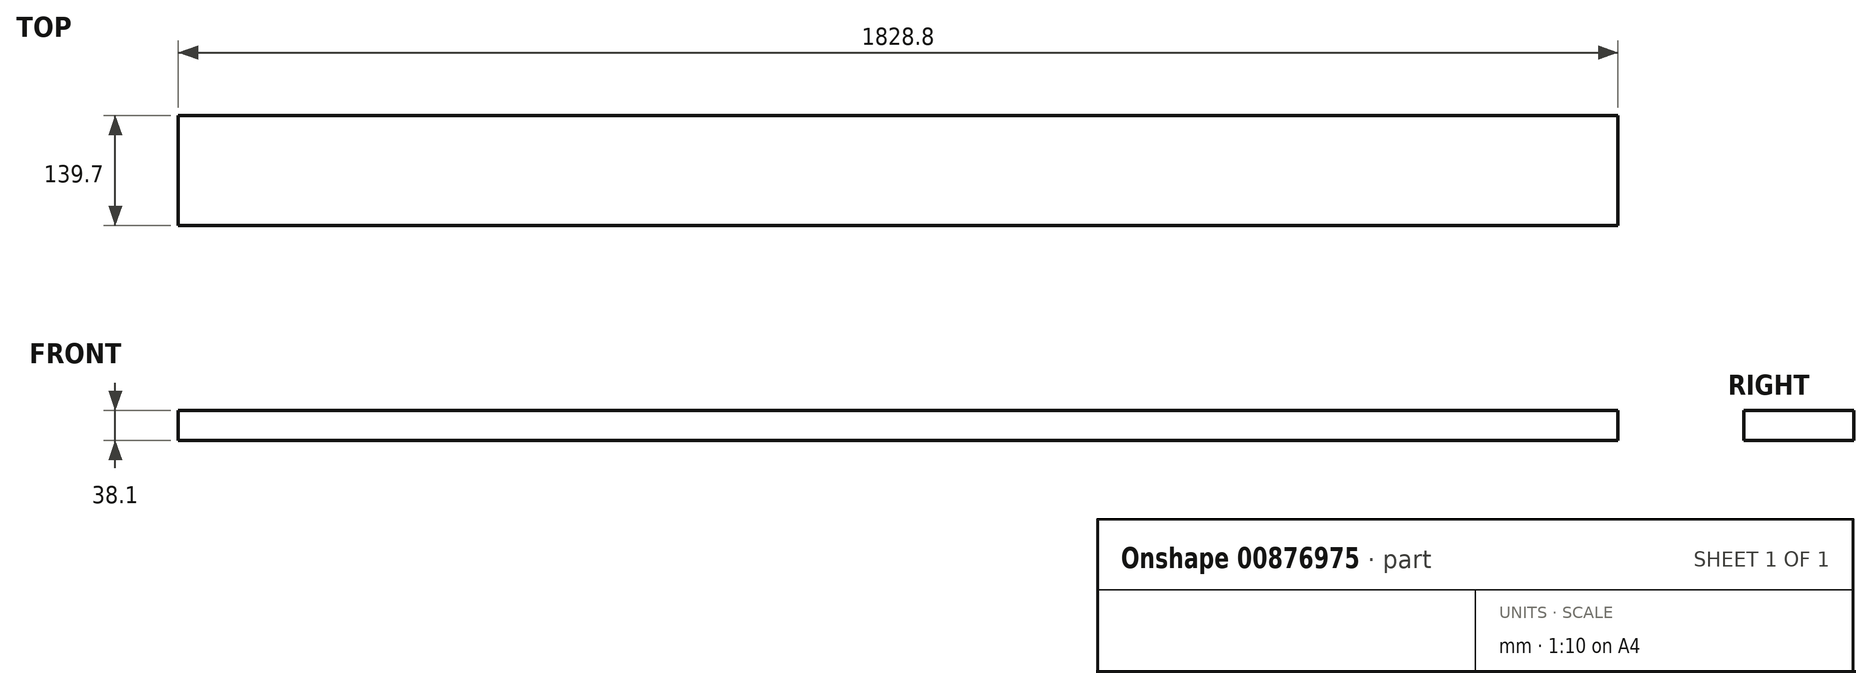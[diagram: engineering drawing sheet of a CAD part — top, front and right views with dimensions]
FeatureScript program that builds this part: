
annotation { "Feature Type Name" : "Feature", "Feature Type Description" : "" }
export const myFeature = defineFeature(function(context is Context, id is Id, definition is map)
    precondition{}
    {
        {
            var Q0;
            Q0=qCreatedBy(makeId("Right.planeOp"),FACE);
            var sketch = newSketch(context, id + "F0", { "sketchPlane" : qUnion([Q0])});
            skLineSegment(sketch, "E0.bottom", {"start": v(69.85, 19.05) * mm, "end": v(-69.85, 19.05) * mm});
            skLineSegment(sketch, "E0.top", {"start": v(69.85, -19.05) * mm, "end": v(-69.85, -19.05) * mm});
            skLineSegment(sketch, "E0.left", {"start": v(69.85, 19.05) * mm, "end": v(69.85, -19.05) * mm});
            skLineSegment(sketch, "E0.right", {"start": v(-69.85, 19.05) * mm, "end": v(-69.85, -19.05) * mm});
            skPoint(sketch, "E0.middle", {"position": v(0, 0) * mm});
            skSolve(sketch);
        }
        {
            var Q0;
            Q0=makeQuery(id+"F0.imprint","IMPRINT",FACE,{"disambiguationData":[TD([[makeQuery(id+"F0.imprint","IMPRINT",EDGE,{"derivedFrom":sQuery(id+"F0.wireOp",EDGE,"E0.bottom")}),1.0]])]});
            extrude(context, id + "F1", {"entities" : qUnion([Q0]), "depth" : 1828.8 * mm, "offsetDistance" : 25.4 * mm});
        }
    });
